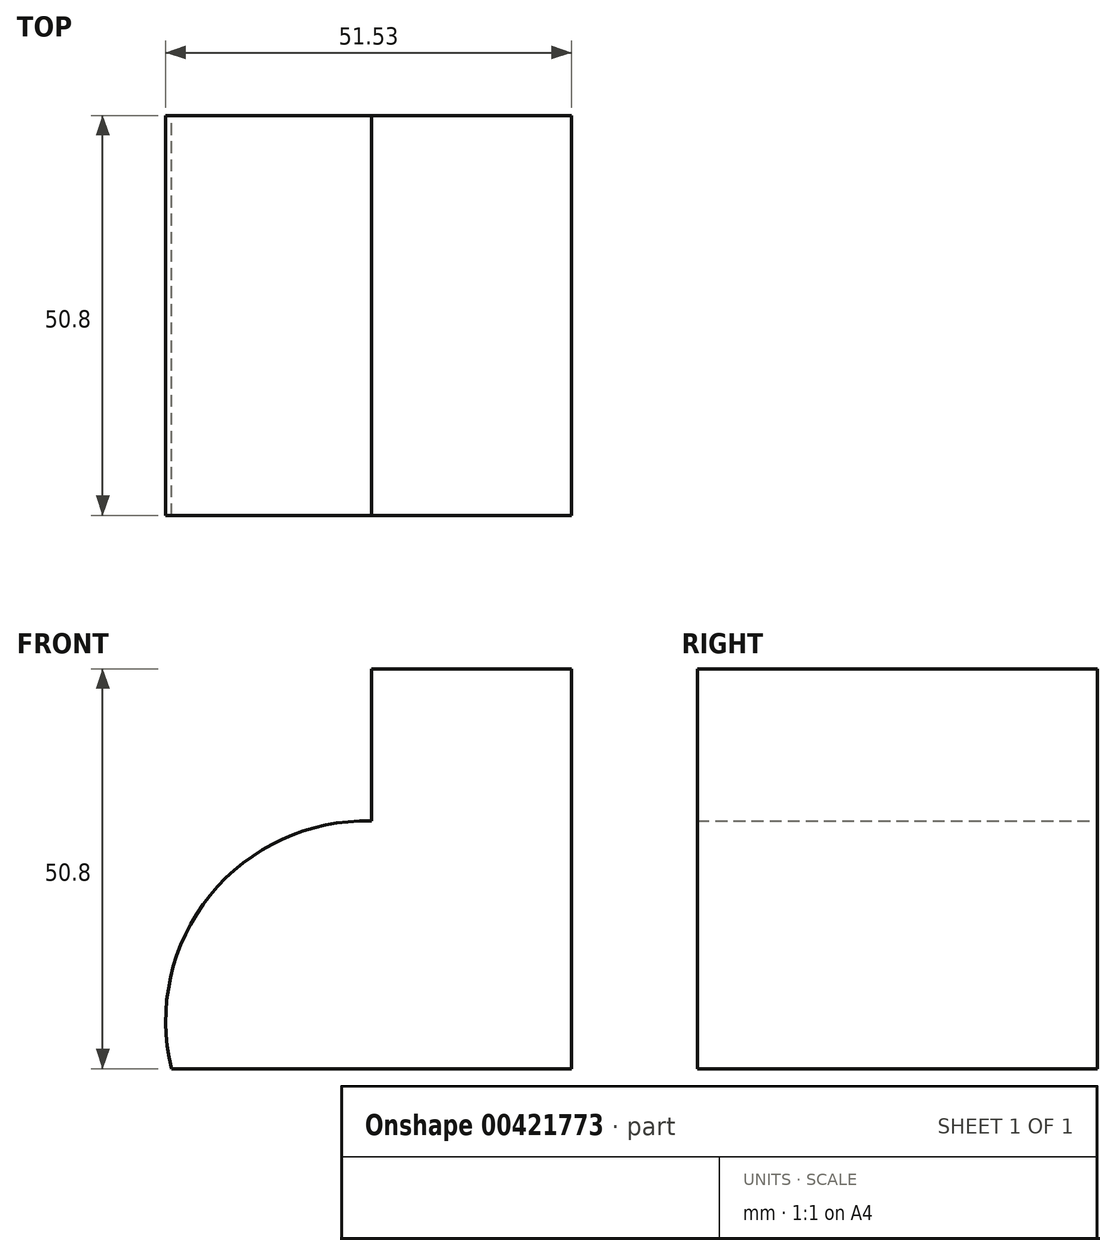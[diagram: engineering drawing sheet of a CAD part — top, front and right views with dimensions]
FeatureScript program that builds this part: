
annotation { "Feature Type Name" : "Feature", "Feature Type Description" : "" }
export const myFeature = defineFeature(function(context is Context, id is Id, definition is map)
    precondition{}
    {
        {
            var Q0;
            Q0=qCreatedBy(makeId("Front.planeOp"),FACE);
            var sketch = newSketch(context, id + "F0", { "sketchPlane" : qUnion([Q0])});
            skLineSegment(sketch, "E0", {"start": v(0, 0) * mm, "end": v(50.8, 0) * mm});
            skLineSegment(sketch, "E1", {"start": v(50.8, 0) * mm, "end": v(50.8, 50.8) * mm});
            skLineSegment(sketch, "E2", {"start": v(50.8, 50.8) * mm, "end": v(25.4, 50.8) * mm});
            skLineSegment(sketch, "E3", {"start": v(25.4, 50.8) * mm, "end": v(25.4, 31.44) * mm});
            skArc(sketch, "E4", {"start": v(25.4, 31.44) * mm, "mid": v(4.9, 22.02) * mm, "end": v(0, 0) * mm});
            skSolve(sketch);
        }
        {
            var Q0;
            Q0=makeQuery(id+"F0.imprint","IMPRINT",FACE,{"disambiguationData":[TD([[makeQuery(id+"F0.imprint","IMPRINT",EDGE,{"derivedFrom":sQuery(id+"F0.wireOp",EDGE,"E0")}),1.0]])]});
            extrude(context, id + "F1", {"entities" : qUnion([Q0]), "depth" : 50.8 * mm});
        }
    });
